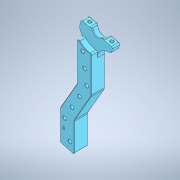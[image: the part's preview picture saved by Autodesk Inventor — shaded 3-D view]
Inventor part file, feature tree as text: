
AUTODESK INVENTOR PART (.ipt)
format: ipt  version: 2021.2 (Build 252289000, 289)  size: 454,656 bytes
history: native  units: mm
features: other x6, fillet x1, chamfer x1
ambient origin geometry x8: Origin, YZ Plane, XZ Plane, XY Plane, X Axis, Y Axis, Z Axis, Center Point
bodies: Body1 (feature_tree)
feature tree (8):
  other  "Твёрдое тело.ipt"
  other  "Непосредственное редактирование1"
  fillet  "Сопряжение1"  Radius=10.0mm
  chamfer  "Фаска1"  [1 undecoded]
  other  "Ножка левая верх::Твёрдое тело.ipt"
  other  "Элемент создания тегов1"
  other  "Твердое тело1"
  other  "Перенос1"
note: 1 required parameter value undecoded (feature->parameter linkage not recoverable at this tier; creation-order binding heuristic only, values carry confidence <= 0.55)
